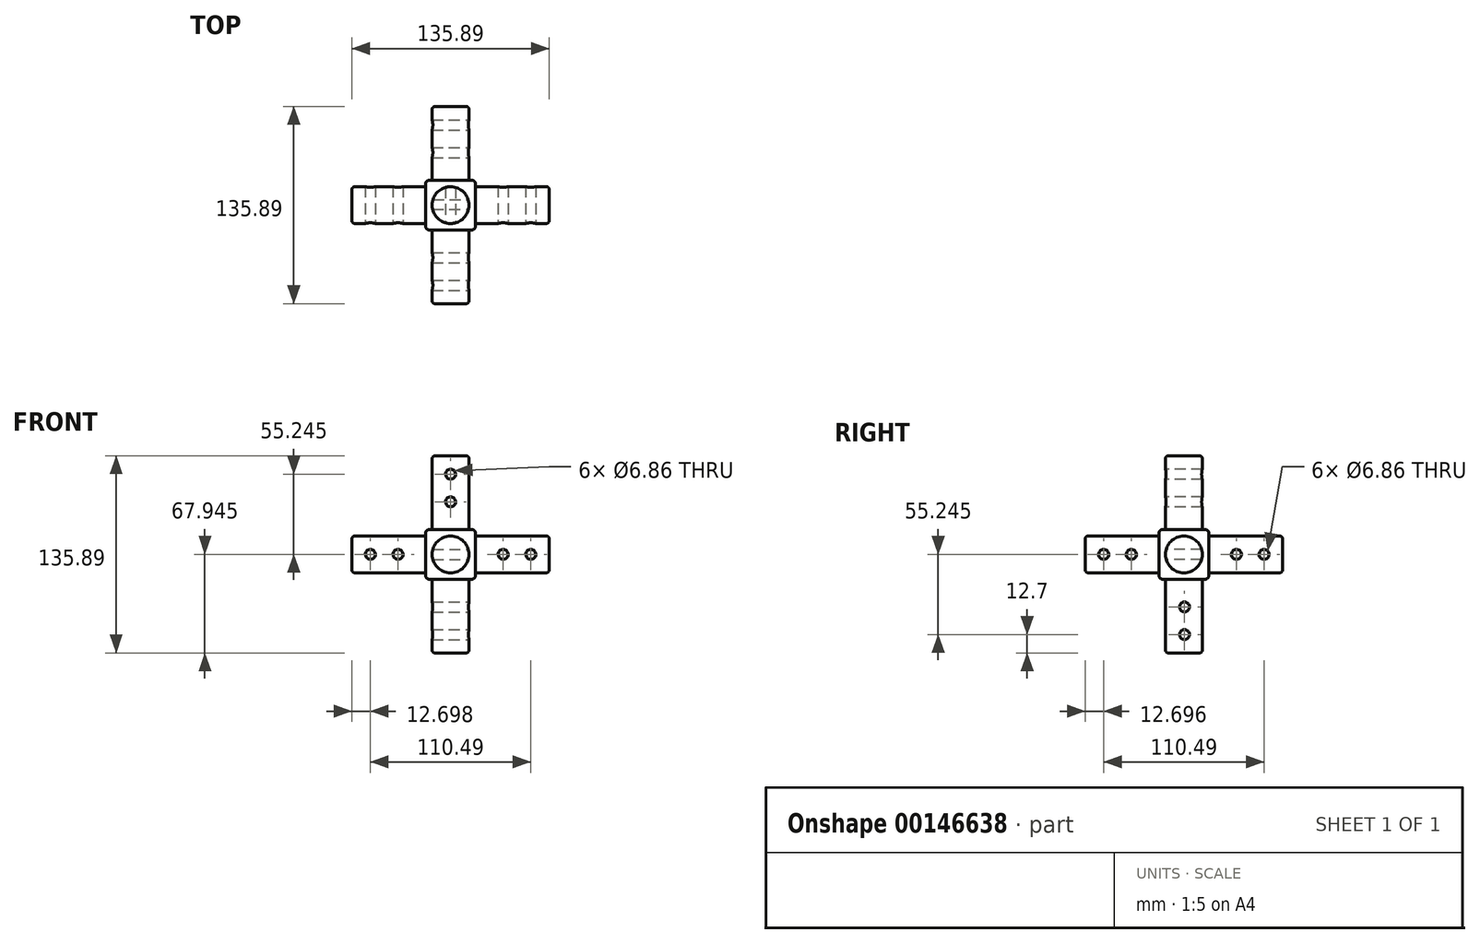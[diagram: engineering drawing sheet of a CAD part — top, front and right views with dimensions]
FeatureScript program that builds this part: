
annotation { "Feature Type Name" : "Feature", "Feature Type Description" : "" }
export const myFeature = defineFeature(function(context is Context, id is Id, definition is map)
    precondition{}
    {
        {
            var Q0;
            Q0=qCreatedBy(makeId("Top.planeOp"),FACE);
            var sketch = newSketch(context, id + "F0", { "sketchPlane" : qUnion([Q0])});
            skLineSegment(sketch, "E0.bottom", {"start": v(-13.47, 23.7) * mm, "end": v(20.82, 23.7) * mm});
            skLineSegment(sketch, "E0.top", {"start": v(-13.47, -10.58) * mm, "end": v(20.82, -10.58) * mm});
            skLineSegment(sketch, "E0.left", {"start": v(-13.47, 23.7) * mm, "end": v(-13.47, -10.58) * mm});
            skLineSegment(sketch, "E0.right", {"start": v(20.82, 23.7) * mm, "end": v(20.82, -10.58) * mm});
            skSolve(sketch);
        }
        {
            var Q0;
            Q0=qSketchRegion(id+"F0",true);
            extrude(context, id + "F1", {"entities" : qUnion([Q0]), "depth" : 34.3 * mm});
        }
        {
            var Q0;
            Q0=makeQuery(id+"F1.opExtrude","CAP_FACE",FACE,{"disambiguationData":[OSD([sQuery(id+"F0.wireOp",EDGE,"E0.bottom"),sQuery(id+"F0.wireOp",EDGE,"E0.top"),sQuery(id+"F0.wireOp",EDGE,"E0.left"),sQuery(id+"F0.wireOp",EDGE,"E0.right")])],"isStart":false});
            var sketch = newSketch(context, id + "F2", { "sketchPlane" : qUnion([Q0])});
            skCircle(sketch, "E1", {"center": v(3.68, 6.56) * mm, "radius": 12.7 * mm});
            skLineSegment(sketch, "E2", {"start": v(3.67, 23.7) * mm, "end": v(3.67, -12.79) * mm, "construction": true});
            skLineSegment(sketch, "E3", {"start": v(20.82, 6.56) * mm, "end": v(-13.47, 6.56) * mm, "construction": true});
            skSolve(sketch);
        }
        {
            var Q0;
            Q0=qSketchRegion(id+"F2",true);
            extrude(context, id + "F3", {"entities" : qUnion([Q0]), "operationType" : NewBodyOperationType.ADD, "depth" : 50.8 * mm});
        }
        {
            var Q0;
            Q0=makeQuery(id+"F1.opExtrude","SWEPT_FACE",FACE,{"disambiguationData":[OSD([sQuery(id+"F0.wireOp",EDGE,"E0.left")])]});
            var sketch = newSketch(context, id + "F4", { "sketchPlane" : qUnion([Q0])});
            skLineSegment(sketch, "E4", {"start": v(-23.7, 17.15) * mm, "end": v(13.45, 17.15) * mm, "construction": true});
            skLineSegment(sketch, "E5", {"start": v(-6.56, 0) * mm, "end": v(-6.56, 34.3) * mm, "construction": true});
            skCircle(sketch, "E6", {"center": v(-6.56, 17.15) * mm, "radius": 12.7 * mm});
            skSolve(sketch);
        }
        {
            var Q0;
            Q0=qSketchRegion(id+"F4",true);
            extrude(context, id + "F5", {"entities" : qUnion([Q0]), "operationType" : NewBodyOperationType.ADD, "depth" : 50.8 * mm});
        }
        {
            var Q0;
            Q0=makeQuery(id+"F1.opExtrude","SWEPT_FACE",FACE,{"disambiguationData":[OSD([sQuery(id+"F0.wireOp",EDGE,"E0.top")])]});
            var sketch = newSketch(context, id + "F6", { "sketchPlane" : qUnion([Q0])});
            skLineSegment(sketch, "E7", {"start": v(-13.47, 17.15) * mm, "end": v(24.43, 17.15) * mm, "construction": true});
            skLineSegment(sketch, "E8", {"start": v(3.67, 0) * mm, "end": v(3.67, 34.3) * mm, "construction": true});
            skCircle(sketch, "E9", {"center": v(3.67, 17.15) * mm, "radius": 12.7 * mm});
            skSolve(sketch);
        }
        {
            var Q0;
            Q0=qSketchRegion(id+"F6",true);
            extrude(context, id + "F7", {"entities" : qUnion([Q0]), "operationType" : NewBodyOperationType.ADD, "depth" : 50.8 * mm});
        }
        {
            var Q0;
            Q0=qCreatedBy(makeId("Front.planeOp"),FACE);
            var sketch = newSketch(context, id + "F8", { "sketchPlane" : qUnion([Q0])});
            skCircle(sketch, "E10", {"center": v(3.67, 53.34) * mm, "radius": 3.43 * mm});
            skCircle(sketch, "E11", {"center": v(3.67, 72.4) * mm, "radius": 3.43 * mm});
            skSolve(sketch);
        }
        {
            var Q0;
            Q0=qSketchRegion(id+"F8",true);
            extrude(context, id + "F9", {"entities" : qUnion([Q0]), "operationType" : NewBodyOperationType.REMOVE, "endBound" : BoundingType.SYMMETRIC, "oppositeDirection" : true, "depth" : 50.8 * mm});
        }
        {
            var Q0;
            Q0=qCreatedBy(makeId("Right.planeOp"),FACE);
            var sketch = newSketch(context, id + "F10", { "sketchPlane" : qUnion([Q0])});
            skCircle(sketch, "E12", {"center": v(-29.63, 17.15) * mm, "radius": 3.43 * mm});
            skCircle(sketch, "E13", {"center": v(-48.68, 17.15) * mm, "radius": 3.43 * mm});
            skSolve(sketch);
        }
        {
            var Q0;
            Q0=qSketchRegion(id+"F10",true);
            extrude(context, id + "F11", {"entities" : qUnion([Q0]), "operationType" : NewBodyOperationType.REMOVE, "endBound" : BoundingType.SYMMETRIC, "oppositeDirection" : true, "depth" : 50.8 * mm});
        }
        {
            var Q0;
            Q0=qCreatedBy(makeId("Front.planeOp"),FACE);
            var sketch = newSketch(context, id + "F12", { "sketchPlane" : qUnion([Q0])});
            skCircle(sketch, "E14", {"center": v(-51.57, 17.15) * mm, "radius": 3.43 * mm});
            skCircle(sketch, "E15", {"center": v(-32.52, 17.15) * mm, "radius": 3.43 * mm});
            skSolve(sketch);
        }
        {
            var Q0;
            Q0=qSketchRegion(id+"F12",true);
            extrude(context, id + "F13", {"entities" : qUnion([Q0]), "operationType" : NewBodyOperationType.REMOVE, "endBound" : BoundingType.SYMMETRIC, "oppositeDirection" : true, "depth" : 50.8 * mm});
        }
        {
            var Q0;
            Q0=makeQuery(id+"F1.opExtrude","SWEPT_EDGE",EDGE,{"disambiguationData":[OSD([sQuery(id+"F0.wireOp",EDGE,"E0.bottom"),sQuery(id+"F0.wireOp",EDGE,"E0.right")])]});
            var Q1;
            Q1=makeQuery(id+"F1.opExtrude","CAP_EDGE",EDGE,{"disambiguationData":[OSD([sQuery(id+"F0.wireOp",EDGE,"E0.right")])],"isStart":false});
            var Q2;
            Q2=makeQuery(id+"F1.opExtrude","SWEPT_EDGE",EDGE,{"disambiguationData":[OSD([sQuery(id+"F0.wireOp",EDGE,"E0.top"),sQuery(id+"F0.wireOp",EDGE,"E0.right")])]});
            var Q3;
            Q3=makeQuery(id+"F1.opExtrude","CAP_EDGE",EDGE,{"disambiguationData":[OSD([sQuery(id+"F0.wireOp",EDGE,"E0.right")])],"isStart":true});
            var Q4;
            Q4=makeQuery(id+"F1.opExtrude","CAP_EDGE",EDGE,{"disambiguationData":[OSD([sQuery(id+"F0.wireOp",EDGE,"E0.bottom")])],"isStart":true});
            var Q5;
            Q5=makeQuery(id+"F1.opExtrude","CAP_EDGE",EDGE,{"disambiguationData":[OSD([sQuery(id+"F0.wireOp",EDGE,"E0.bottom")])],"isStart":false});
            var Q6;
            Q6=makeQuery(id+"F1.opExtrude","SWEPT_EDGE",EDGE,{"disambiguationData":[OSD([sQuery(id+"F0.wireOp",EDGE,"E0.bottom"),sQuery(id+"F0.wireOp",EDGE,"E0.left")])]});
            var Q7;
            Q7=makeQuery(id+"F1.opExtrude","CAP_EDGE",EDGE,{"disambiguationData":[OSD([sQuery(id+"F0.wireOp",EDGE,"E0.left")])],"isStart":true});
            var Q8;
            Q8=makeQuery(id+"F1.opExtrude","CAP_EDGE",EDGE,{"disambiguationData":[OSD([sQuery(id+"F0.wireOp",EDGE,"E0.top")])],"isStart":true});
            var Q9;
            Q9=makeQuery(id+"F1.opExtrude","CAP_EDGE",EDGE,{"disambiguationData":[OSD([sQuery(id+"F0.wireOp",EDGE,"E0.left")])],"isStart":false});
            var Q10;
            Q10=makeQuery(id+"F1.opExtrude","SWEPT_EDGE",EDGE,{"disambiguationData":[OSD([sQuery(id+"F0.wireOp",EDGE,"E0.top"),sQuery(id+"F0.wireOp",EDGE,"E0.left")])]});
            var Q11;
            Q11=makeQuery(id+"F1.opExtrude","CAP_EDGE",EDGE,{"disambiguationData":[OSD([sQuery(id+"F0.wireOp",EDGE,"E0.top")])],"isStart":false});
            fillet(context, id + "F14", {"entities" : qUnion([Q0, Q1, Q2, Q3, Q4, Q5, Q6, Q7, Q8, Q9, Q10, Q11]), "radius" : 2.54 * mm, "tangentPropagation" : true, "allowEdgeOverflow" : false});
        }
        {
            var Q0;
            Q0=makeQuery(id+"F1.opExtrude","SWEPT_FACE",FACE,{"disambiguationData":[OSD([sQuery(id+"F0.wireOp",EDGE,"E0.bottom")])]});
            var sketch = newSketch(context, id + "F15", { "sketchPlane" : qUnion([Q0])});
            skLineSegment(sketch, "E16", {"start": v(-18.28, 17.15) * mm, "end": v(4.82, 17.15) * mm, "construction": true});
            skPoint(sketch, "E16.endSnap0", {"position": v(-18.28, 17.15) * mm});
            skLineSegment(sketch, "E17", {"start": v(-3.67, 31.75) * mm, "end": v(-3.67, 14.65) * mm, "construction": true});
            skCircle(sketch, "E18", {"center": v(-3.67, 17.15) * mm, "radius": 12.7 * mm});
            skSolve(sketch);
        }
        {
            var Q0;
            Q0=qSketchRegion(id+"F15",true);
            extrude(context, id + "F16", {"entities" : qUnion([Q0]), "operationType" : NewBodyOperationType.ADD, "depth" : 50.8 * mm});
        }
        {
            var Q0;
            Q0=qCreatedBy(makeId("Right.planeOp"),FACE);
            var sketch = newSketch(context, id + "F17", { "sketchPlane" : qUnion([Q0])});
            skCircle(sketch, "E19", {"center": v(42.76, 17.15) * mm, "radius": 3.43 * mm});
            skCircle(sketch, "E20", {"center": v(61.8, 17.15) * mm, "radius": 3.43 * mm});
            skSolve(sketch);
        }
        {
            var Q0;
            Q0=qSketchRegion(id+"F17",true);
            extrude(context, id + "F18", {"entities" : qUnion([Q0]), "operationType" : NewBodyOperationType.REMOVE, "endBound" : BoundingType.SYMMETRIC, "oppositeDirection" : true, "depth" : 50.8 * mm});
        }
        {
            var Q0;
            Q0=makeQuery(id+"F1.opExtrude","SWEPT_FACE",FACE,{"disambiguationData":[OSD([sQuery(id+"F0.wireOp",EDGE,"E0.right")])]});
            var sketch = newSketch(context, id + "F19", { "sketchPlane" : qUnion([Q0])});
            skCircle(sketch, "E21", {"center": v(6.56, 17.14) * mm, "radius": 12.7 * mm});
            skLineSegment(sketch, "E22", {"start": v(-8.04, 17.15) * mm, "end": v(28.63, 17.15) * mm, "construction": true});
            skLineSegment(sketch, "E23", {"start": v(6.56, 2.54) * mm, "end": v(6.56, 27.82) * mm, "construction": true});
            skSolve(sketch);
        }
        {
            var Q0;
            Q0=qSketchRegion(id+"F19",true);
            extrude(context, id + "F20", {"entities" : qUnion([Q0]), "operationType" : NewBodyOperationType.ADD, "depth" : 50.8 * mm});
        }
        {
            var Q0;
            Q0=qCreatedBy(makeId("Front.planeOp"),FACE);
            var sketch = newSketch(context, id + "F21", { "sketchPlane" : qUnion([Q0])});
            skCircle(sketch, "E24", {"center": v(58.92, 17.15) * mm, "radius": 3.43 * mm});
            skCircle(sketch, "E25", {"center": v(39.87, 17.15) * mm, "radius": 3.43 * mm});
            skSolve(sketch);
        }
        {
            var Q0;
            Q0=qSketchRegion(id+"F21",true);
            extrude(context, id + "F22", {"entities" : qUnion([Q0]), "operationType" : NewBodyOperationType.REMOVE, "endBound" : BoundingType.SYMMETRIC, "oppositeDirection" : true, "depth" : 50.8 * mm});
        }
        {
            var Q0;
            Q0=makeQuery(id+"F1.opExtrude","CAP_FACE",FACE,{"disambiguationData":[OSD([sQuery(id+"F0.wireOp",EDGE,"E0.bottom"),sQuery(id+"F0.wireOp",EDGE,"E0.top"),sQuery(id+"F0.wireOp",EDGE,"E0.left"),sQuery(id+"F0.wireOp",EDGE,"E0.right")])],"isStart":true});
            var sketch = newSketch(context, id + "F23", { "sketchPlane" : qUnion([Q0])});
            skCircle(sketch, "E26", {"center": v(3.67, -6.56) * mm, "radius": 12.7 * mm});
            skPoint(sketch, "E26.centerSnap0", {"position": v(3.67, -21.17) * mm});
            skPoint(sketch, "E26.centerSnap1", {"position": v(18.28, -6.56) * mm});
            skSolve(sketch);
        }
        {
            var Q0;
            Q0 = qSketchRegion(id + "F23", true);
            extrude(context, id + "F24", {"entities" : qUnion([Q0]), "operationType" : NewBodyOperationType.ADD, "depth" : 50.8 * mm});
        }
        {
            var Q0;
            Q0=makeQuery(id+"F3.opExtrude","CAP_EDGE",EDGE,{"disambiguationData":[OSD([sQuery(id+"F2.wireOp",EDGE,"E1")])],"isStart":false});
            var Q1;
            Q1=makeQuery(id+"F7.opExtrude","CAP_EDGE",EDGE,{"disambiguationData":[OSD([sQuery(id+"F6.wireOp",EDGE,"E9")])],"isStart":false});
            var Q2;
            Q2=makeQuery(id+"F5.opExtrude","CAP_EDGE",EDGE,{"disambiguationData":[OSD([sQuery(id+"F4.wireOp",EDGE,"E6")])],"isStart":false});
            var Q3;
            Q3=makeQuery(id+"F16.opExtrude","CAP_EDGE",EDGE,{"disambiguationData":[OSD([sQuery(id+"F15.wireOp",EDGE,"E18")])],"isStart":false});
            var Q4;
            Q4=makeQuery(id+"F20.opExtrude","CAP_EDGE",EDGE,{"disambiguationData":[OSD([sQuery(id+"F19.wireOp",EDGE,"E21")])],"isStart":false});
            var Q5;
            Q5=makeQuery(id+"F24.opExtrude","CAP_EDGE",EDGE,{"disambiguationData":[OSD([sQuery(id+"F23.wireOp",EDGE,"E26")])],"isStart":false});
            fillet(context, id + "F25", {"entities" : qUnion([Q0, Q1, Q2, Q3, Q4, Q5]), "radius" : 2.03 * mm, "tangentPropagation" : true, "allowEdgeOverflow" : false});
        }
        {
            var Q0;
            Q0=qCreatedBy(makeId("Right.planeOp"),FACE);
            var sketch = newSketch(context, id + "F26", { "sketchPlane" : qUnion([Q0])});
            skCircle(sketch, "E27", {"center": v(7.01, -19.05) * mm, "radius": 3.43 * mm});
            skCircle(sketch, "E28", {"center": v(7.01, -38.1) * mm, "radius": 3.43 * mm});
            skSolve(sketch);
        }
        {
            var Q0;
            Q0 = qSketchRegion(id + "F26", true);
            extrude(context, id + "F27", {"entities" : qUnion([Q0]), "operationType" : NewBodyOperationType.REMOVE, "endBound" : BoundingType.SYMMETRIC, "oppositeDirection" : true, "depth" : 50.8 * mm});
        }
    });
